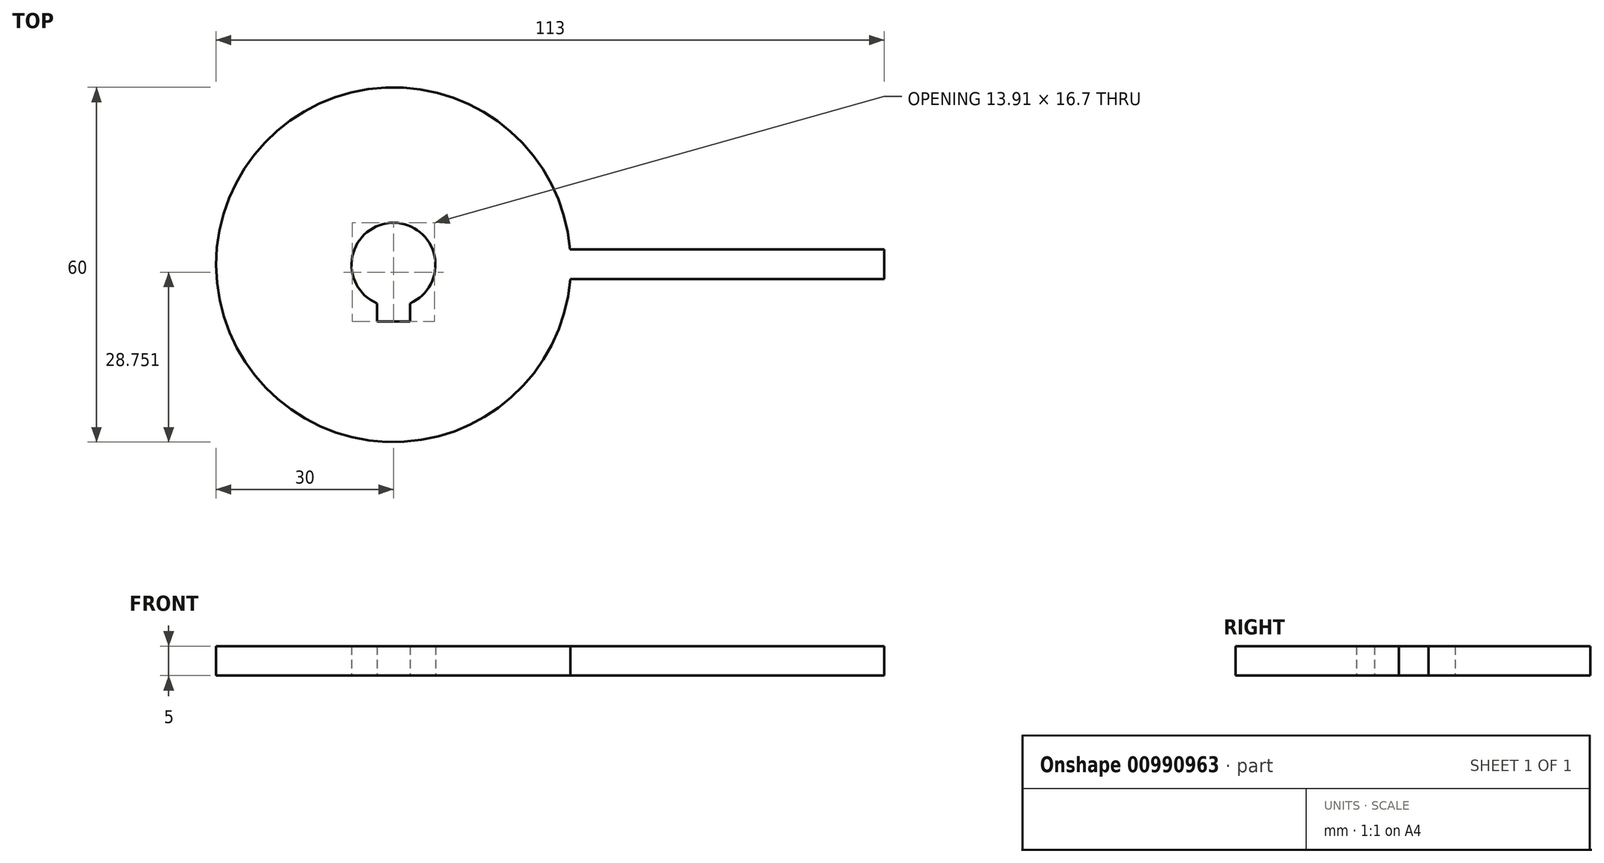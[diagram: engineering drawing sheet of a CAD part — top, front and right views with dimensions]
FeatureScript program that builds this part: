
annotation { "Feature Type Name" : "Feature", "Feature Type Description" : "" }
export const myFeature = defineFeature(function(context is Context, id is Id, definition is map)
    precondition{}
    {
        {
            var Q0;
            Q0=qCreatedBy(makeId("Top.planeOp"),FACE);
            var sketch = newSketch(context, id + "F0", { "sketchPlane" : qUnion([Q0])});
            skCircle(sketch, "E0", {"center": v(0, -0.09) * mm, "radius": 7.1 * mm});
            skLineSegment(sketch, "E1", {"start": v(0, -0.09) * mm, "end": v(0, -9.69) * mm, "construction": true});
            skLineSegment(sketch, "E2", {"start": v(0, -9.69) * mm, "end": v(-2.8, -9.69) * mm});
            skLineSegment(sketch, "E3", {"start": v(-2.8, -9.69) * mm, "end": v(-2.8, -6.61) * mm});
            skCircle(sketch, "E4", {"center": v(0, -0.09) * mm, "radius": 30 * mm});
            skLineSegment(sketch, "E5.MirrorCS", {"start": v(0, -9.69) * mm, "end": v(2.8, -9.69) * mm});
            skLineSegment(sketch, "E6.MirrorCS", {"start": v(2.8, -9.69) * mm, "end": v(2.8, -6.61) * mm});
            skPoint(sketch, "E7", {"position": v(0, -7.19) * mm});
            skLineSegment(sketch, "E8", {"start": v(0, 0) * mm, "end": v(87.03, 0) * mm, "construction": true});
            skLineSegment(sketch, "E9", {"start": v(82.99, 0) * mm, "end": v(82.99, 2.5) * mm});
            skLineSegment(sketch, "E10", {"start": v(82.99, 2.5) * mm, "end": v(29.88, 2.5) * mm});
            skPoint(sketch, "E11", {"position": v(29.99, 0) * mm});
            skLineSegment(sketch, "E12.MirrorCS", {"start": v(82.99, -2.5) * mm, "end": v(29.88, -2.5) * mm});
            skLineSegment(sketch, "E13.MirrorCS", {"start": v(82.99, 0) * mm, "end": v(82.99, -2.5) * mm});
            skSolve(sketch);
        }
        {
            var Q0;
            Q0=makeQuery(id+"F0.imprint","IMPRINT",FACE,{"disambiguationData":[TD([[makeQuery(id+"F0.imprint","IMPRINT",EDGE,{"derivedFrom":sQuery(id+"F0.wireOp",EDGE,"E2")}),1.0]])]});
            var Q1;
            Q1=makeQuery(id+"F0.imprint","IMPRINT",FACE,{"disambiguationData":[TD([[makeQuery(id+"F0.imprint","IMPRINT",EDGE,{"derivedFrom":sQuery(id+"F0.wireOp",EDGE,"E9")}),1.0]])]});
            extrude(context, id + "F1", {"entities" : qUnion([Q0, Q1]), "depth" : 5 * mm, "offsetDistance" : 25 * mm});
        }
    });
